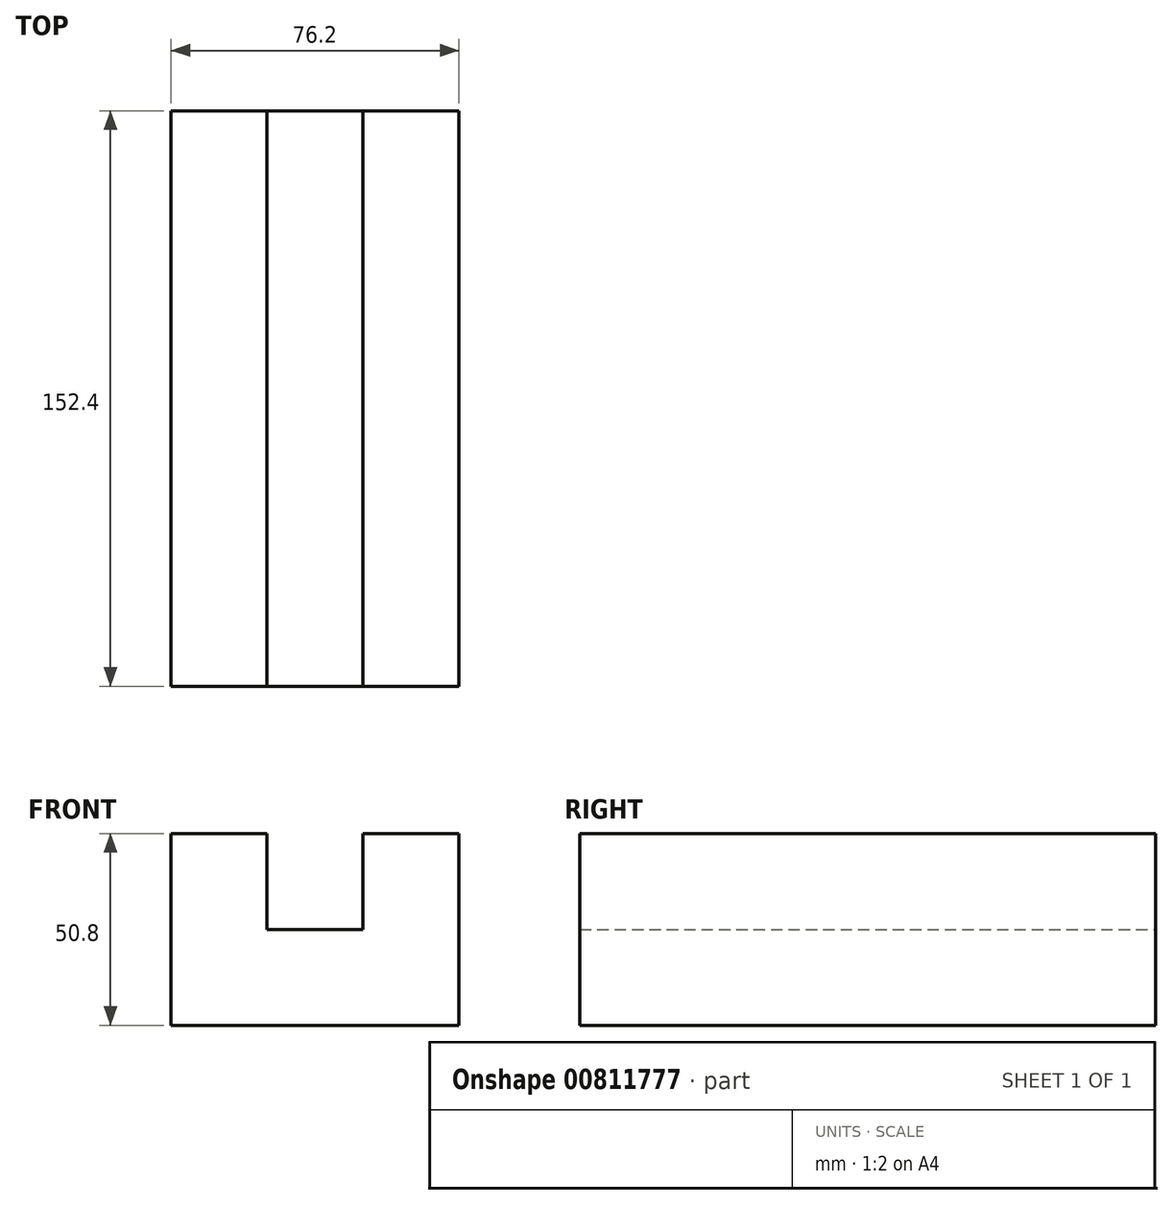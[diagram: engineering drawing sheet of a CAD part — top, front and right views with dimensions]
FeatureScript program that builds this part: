
annotation { "Feature Type Name" : "Feature", "Feature Type Description" : "" }
export const myFeature = defineFeature(function(context is Context, id is Id, definition is map)
    precondition{}
    {
        {
            var Q0;
            Q0=qCreatedBy(makeId("Front.planeOp"),FACE);
            var sketch = newSketch(context, id + "F0", { "sketchPlane" : qUnion([Q0])});
            skLineSegment(sketch, "E0", {"start": v(0, 0) * mm, "end": v(76.2, 0) * mm});
            skLineSegment(sketch, "E1", {"start": v(0, 0) * mm, "end": v(0, 50.8) * mm});
            skLineSegment(sketch, "E2", {"start": v(76.2, 0) * mm, "end": v(76.2, 50.8) * mm});
            skLineSegment(sketch, "E3", {"start": v(0, 50.8) * mm, "end": v(25.4, 50.8) * mm});
            skLineSegment(sketch, "E4", {"start": v(76.2, 50.8) * mm, "end": v(50.8, 50.8) * mm});
            skLineSegment(sketch, "E5", {"start": v(50.8, 50.8) * mm, "end": v(50.8, 25.4) * mm});
            skLineSegment(sketch, "E6", {"start": v(50.8, 25.4) * mm, "end": v(25.4, 25.4) * mm});
            skLineSegment(sketch, "E7", {"start": v(25.4, 25.4) * mm, "end": v(25.4, 50.8) * mm});
            skSolve(sketch);
        }
        {
            var Q0;
            Q0=makeQuery(id+"F0.imprint","IMPRINT",FACE,{"disambiguationData":[TD([[makeQuery(id+"F0.imprint","IMPRINT",EDGE,{"derivedFrom":sQuery(id+"F0.wireOp",EDGE,"E0")}),1.0]])]});
            extrude(context, id + "F1", {"entities" : qUnion([Q0]), "depth" : 152.4 * mm, "offsetDistance" : 25.4 * mm});
        }
    });
